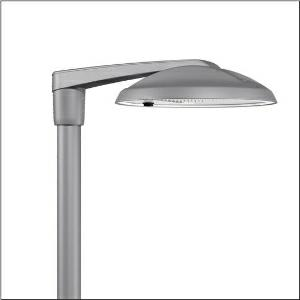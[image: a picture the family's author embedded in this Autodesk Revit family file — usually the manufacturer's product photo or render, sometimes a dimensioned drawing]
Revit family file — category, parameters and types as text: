
# Revit family: dl_r__50_iq_mini___st1_0a_5xa248d31u08le_9cf4
name_source: partatom
category: Lighting Fixtures
units: mm (PartAtom-declared; Revit-internal decimal feet)

## family parameters
Cut with Voids When Loaded = No
Host = Face
Light Source = No
Part Type = Normal
Room Calculation Point = No
Round Connector Dimension = Use Diameter
Shared = No

## types (1)
- --- (1 x LED, 10390 lm, 66 W, 3000K)
    Apparent Load = 66 VA
    CIE Flux Codes = 37 72 97 100 100
    Color Rendering = 70
    Color Temperature = 3000K
    Default Elevation = 1800 mm
    Description = DL® 50 iQ mini, mast luminaire, primary light control with lens, of PMMA, primary optical cover: cover, of toughened safety glass, transparent, light distribution: ST1.0a, light emission: direct distribution, primary light characteristic: asymmetric, installation type: post-top, side-entry, LED, High Power LED, rated luminous flux: 10.390lm, luminous efficacy: 157lm/W, light colour: 730, colour temperature: 3000K, control gear: iQ-Street Remote, D4i with power reduction, control: optimised constant luminous flux control (CLO 2.0), Desk-Remote (wireless, voltage-free reading and setting of iQ features in the workshop via application-optimized NFC function/RFID function), Light-Fading, Smart-Wire, Night-Set, Lumen-Switch, Temp-Guard, Auto-Match, Street-Remote, pre-setting: logarithmic dimming characteristic, mains connection: 220..240V, AC, 50/60Hz, connection cable pre-assembled, cable length: 8,5m, start of lifetime: 66W, end of service life: 69W, reduction: 30W, luminaire housing, of diecast aluminium, powder-coated, Siteco® metallic grey (DB 702S), inclination adjustable: 0°, 5°, 10° (post-top) | 0°, -5°, -10°, -15° (side-entry), please order mast post-top element or mast side-entry element separately, diameter: 500mm, height: 115mm, post-top: for spigot size d x l = 76 x 100mm; with reducer (optional accessory) 60 x 100mm | side-entry: for spigot size d x l = 60 x 100mm; with reducer (optional accessory) 42 x 100mm, mounting height: 4..6m, Smart Interface below, protection rating (complete): IP66, insulation class (complete): insulation class II (safety insulation), certification: CE, ENEC, ENEC+, VDE, impact resistance: IK08, permissible operating ambient temperature for outdoor applications: -25..+40°C, standard-compliant lighting for roads and squares, packaging unit: 1 piece

Light Distribution: ST1.0a
    Height = 115 mm
    Lamp = 1 x LED
    Lamp Light Flux = 10390 lm
    Lamp Power = 66 W
    Lamp count = 1
    Length = 500 mm
    Luminous efficacy = 157 lm/W
    Manufacturer = Siteco
    ModVariant = No
    Model = 5XA248D31U08LE
    Number of Poles = 1
    OnlyDefault = Yes
    Power Factor = 1
    Product Name = DL® 50 iQ mini | ST1.0a
    Product group = mast luminaire | pylon top
    ProductGroupID = 6100
    Protection Class = Protection class II
    Protection Degree = IP 66
    RLX_Detail_Level = 1
    RLX_Emergency_Light_Flux = 0 lm
    RLX_Emergency_Type = 0
    RLX_Emergency_Type_DB = No
    RlxData = <blob elided: 106565 chars, md5=324ff0b4>
    Socket = socket
    Standby Power = 0 W
    System Light Flux = 10390 lm
    System Power = 66 W
    Type Comments = factory setting: luminous flux: 100 % | dim-lin: 254 | 691 mA
    Type Image = l_1296955.jpg
    URL = http://relux.com
    VarID = @adj_087035
    Voltage = 0 V
    Weight = 0.00 kg
    Width = 0 mm  [stored 0 ft]

note: [stored X ft] marks values corroborated as IEEE doubles in the binary element streams (Revit-internal decimal feet)

## geometry (parser evidence)
native form markers: Blend x4, Sweep x9
no freeform markers — native parametric forms only
